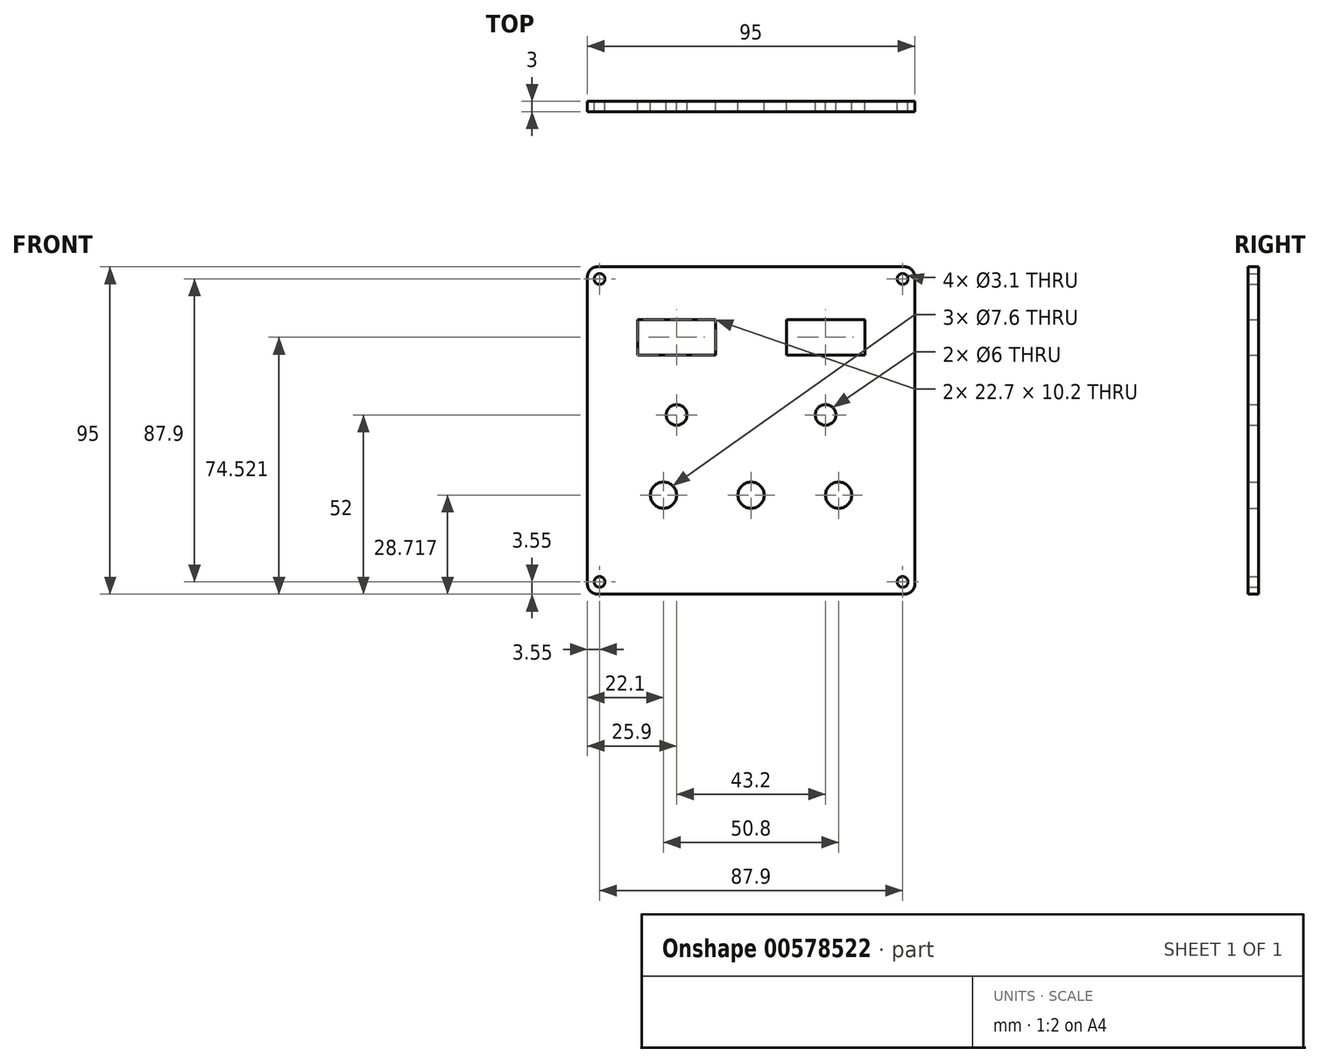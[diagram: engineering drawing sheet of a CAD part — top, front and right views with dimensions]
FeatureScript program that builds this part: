
annotation { "Feature Type Name" : "Feature", "Feature Type Description" : "" }
export const myFeature = defineFeature(function(context is Context, id is Id, definition is map)
    precondition{}
    {
        {
            var Q0;
            Q0=qCreatedBy(makeId("Front.planeOp"),FACE);
            var sketch = newSketch(context, id + "F0", { "sketchPlane" : qUnion([Q0])});
            skLineSegment(sketch, "E0.bottom", {"start": v(44.5, -47.5) * mm, "end": v(-44.5, -47.5) * mm});
            skLineSegment(sketch, "E0.top", {"start": v(44.5, 47.5) * mm, "end": v(-44.5, 47.5) * mm});
            skLineSegment(sketch, "E0.left", {"start": v(47.5, -44.5) * mm, "end": v(47.5, 44.5) * mm});
            skLineSegment(sketch, "E0.right", {"start": v(-47.5, -44.5) * mm, "end": v(-47.5, 44.5) * mm});
            skPoint(sketch, "E0.middle", {"position": v(0, 0) * mm});
            skCircle(sketch, "E1", {"center": v(21.6, 4.5) * mm, "radius": 3 * mm});
            skCircle(sketch, "E2", {"center": v(-21.6, 4.5) * mm, "radius": 3 * mm});
            skLineSegment(sketch, "E3.bottom", {"start": v(32.95, 21.92) * mm, "end": v(10.25, 21.92) * mm});
            skLineSegment(sketch, "E3.top", {"start": v(32.95, 32.12) * mm, "end": v(10.25, 32.12) * mm});
            skLineSegment(sketch, "E3.left", {"start": v(32.95, 21.92) * mm, "end": v(32.95, 32.12) * mm});
            skLineSegment(sketch, "E3.right", {"start": v(10.25, 21.92) * mm, "end": v(10.25, 32.12) * mm});
            skPoint(sketch, "E3.middle", {"position": v(21.6, 27.02) * mm});
            skPoint(sketch, "E4", {"position": v(-21.6, 27.02) * mm});
            skLineSegment(sketch, "E5.bottom", {"start": v(-10.25, 21.92) * mm, "end": v(-32.95, 21.92) * mm});
            skLineSegment(sketch, "E5.top", {"start": v(-10.25, 32.12) * mm, "end": v(-32.95, 32.12) * mm});
            skLineSegment(sketch, "E5.left", {"start": v(-10.25, 21.92) * mm, "end": v(-10.25, 32.12) * mm});
            skLineSegment(sketch, "E5.right", {"start": v(-32.95, 21.92) * mm, "end": v(-32.95, 32.12) * mm});
            skPoint(sketch, "E6", {"position": v(0, -18.78) * mm});
            skPoint(sketch, "E7", {"position": v(-25.4, -18.78) * mm});
            skPoint(sketch, "E8", {"position": v(25.4, -18.78) * mm});
            skCircle(sketch, "E9", {"center": v(-25.4, -18.78) * mm, "radius": 3.8 * mm});
            skCircle(sketch, "E10", {"center": v(0, -18.78) * mm, "radius": 3.8 * mm});
            skCircle(sketch, "E11", {"center": v(25.4, -18.78) * mm, "radius": 3.8 * mm});
            skPoint(sketch, "E12.visualSharp", {"position": v(47.5, -47.5) * mm});
            skArc(sketch, "E12.filletArc", {"start": v(44.5, -47.5) * mm, "mid": v(46.62, -46.62) * mm, "end": v(47.5, -44.5) * mm});
            skPoint(sketch, "E13.visualSharp", {"position": v(-47.5, 47.5) * mm});
            skArc(sketch, "E13.filletArc", {"start": v(-44.5, 47.5) * mm, "mid": v(-46.62, 46.62) * mm, "end": v(-47.5, 44.5) * mm});
            skPoint(sketch, "E14.visualSharp", {"position": v(47.5, 47.5) * mm});
            skArc(sketch, "E14.filletArc", {"start": v(47.5, 44.5) * mm, "mid": v(46.62, 46.62) * mm, "end": v(44.5, 47.5) * mm});
            skPoint(sketch, "E15.visualSharp", {"position": v(-47.5, -47.5) * mm});
            skArc(sketch, "E15.filletArc", {"start": v(-47.5, -44.5) * mm, "mid": v(-46.62, -46.62) * mm, "end": v(-44.5, -47.5) * mm});
            skCircle(sketch, "E16", {"center": v(-43.95, -43.95) * mm, "radius": 1.55 * mm});
            skCircle(sketch, "E17", {"center": v(43.95, -43.95) * mm, "radius": 1.55 * mm});
            skCircle(sketch, "E18", {"center": v(43.95, 43.95) * mm, "radius": 1.55 * mm});
            skCircle(sketch, "E19", {"center": v(-43.95, 43.95) * mm, "radius": 1.55 * mm});
            skSolve(sketch);
        }
        {
            var Q0;
            Q0 = qSketchRegion(id + "F0", true);
            extrude(context, id + "F1", {"entities" : qUnion([Q0]), "depth" : 3 * mm, "offsetDistance" : 25 * mm});
        }
    });
